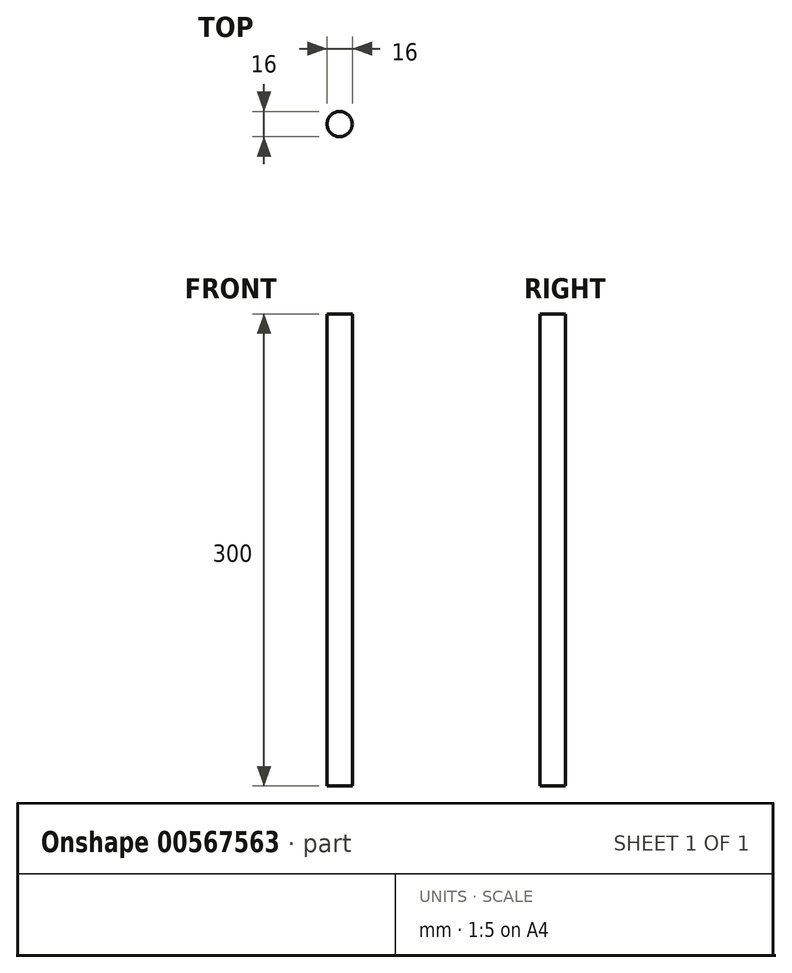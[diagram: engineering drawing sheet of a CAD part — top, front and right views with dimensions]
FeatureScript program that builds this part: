
annotation { "Feature Type Name" : "Feature", "Feature Type Description" : "" }
export const myFeature = defineFeature(function(context is Context, id is Id, definition is map)
    precondition{}
    {
        {
            var Q0;
            Q0=qCreatedBy(makeId("Top.planeOp"),FACE);
            var sketch = newSketch(context, id + "F0", { "sketchPlane" : qUnion([Q0])});
            skCircle(sketch, "E0", {"center": v(0, 0) * mm, "radius": 8 * mm});
            skSolve(sketch);
        }
        {
            var Q0;
            Q0=makeQuery(id+"F0.imprint","IMPRINT",FACE,{"disambiguationData":[TD([[makeQuery(id+"F0.imprint","IMPRINT",EDGE,{"derivedFrom":sQuery(id+"F0.wireOp",EDGE,"E0")}),1.0]])]});
            extrude(context, id + "F1", {"entities" : qUnion([Q0]), "depth" : 300 * mm, "offsetDistance" : 25 * mm});
        }
    });
